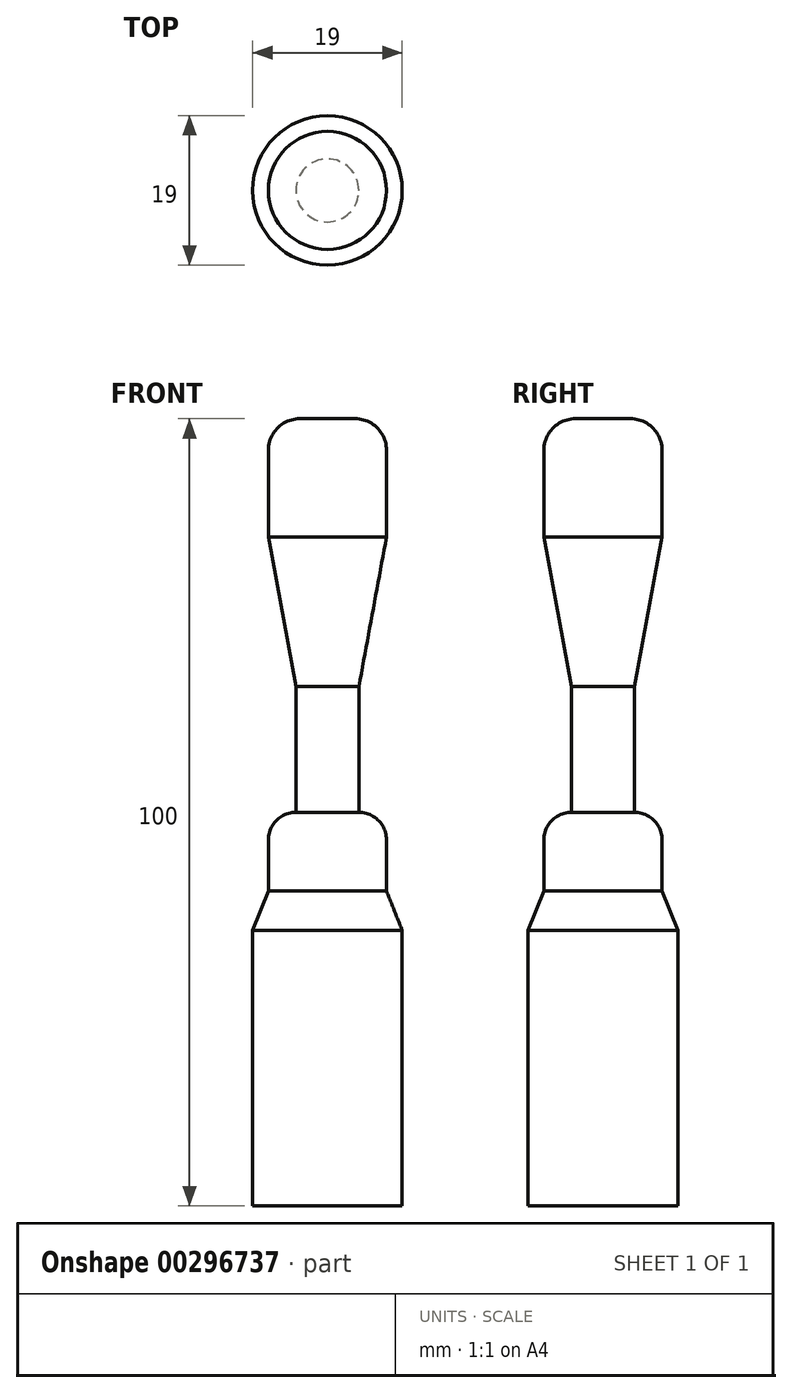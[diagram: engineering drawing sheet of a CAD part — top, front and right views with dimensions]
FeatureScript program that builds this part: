
annotation { "Feature Type Name" : "Feature", "Feature Type Description" : "" }
export const myFeature = defineFeature(function(context is Context, id is Id, definition is map)
    precondition{}
    {
        {
            var Q0;
            Q0=qCreatedBy(makeId("Front.planeOp"),FACE);
            var sketch = newSketch(context, id + "F0", { "sketchPlane" : qUnion([Q0])});
            skLineSegment(sketch, "E0", {"start": v(0, 0) * mm, "end": v(0, -100) * mm});
            skLineSegment(sketch, "E1", {"start": v(0, -100) * mm, "end": v(9.5, -100) * mm});
            skLineSegment(sketch, "E2", {"start": v(9.5, -100) * mm, "end": v(9.5, -65) * mm});
            skLineSegment(sketch, "E3", {"start": v(9.5, -65) * mm, "end": v(7.5, -60) * mm});
            skLineSegment(sketch, "E4", {"start": v(7.5, -60) * mm, "end": v(7.5, -53.5) * mm});
            skArc(sketch, "E5", {"start": v(7.5, -53.5) * mm, "mid": v(6.47, -51.03) * mm, "end": v(4, -50) * mm});
            skLineSegment(sketch, "E6", {"start": v(4, -50) * mm, "end": v(4, -34) * mm});
            skLineSegment(sketch, "E7", {"start": v(4, -34) * mm, "end": v(7.5, -15) * mm});
            skLineSegment(sketch, "E8", {"start": v(7.5, -15) * mm, "end": v(7.5, -4) * mm});
            skArc(sketch, "E9", {"start": v(7.5, -4) * mm, "mid": v(6.33, -1.17) * mm, "end": v(3.5, 0) * mm});
            skLineSegment(sketch, "E10", {"start": v(0, 0) * mm, "end": v(3.5, 0) * mm});
            skSolve(sketch);
        }
        {
            var Q0;
            Q0=makeQuery(id+"F0.imprint","IMPRINT",FACE,{"disambiguationData":[TD([[makeQuery(id+"F0.imprint","IMPRINT",EDGE,{"derivedFrom":sQuery(id+"F0.wireOp",EDGE,"E0")}),1.0]])]});
            var Q1;
            Q1=sQuery(id+"F0.wireOp",EDGE,"E0");
            revolve(context, id + "F1", {"entities" : qUnion([Q0]), "axis" : qUnion([Q1]), "revolveType" : RevolveType.FULL});
        }
    });
